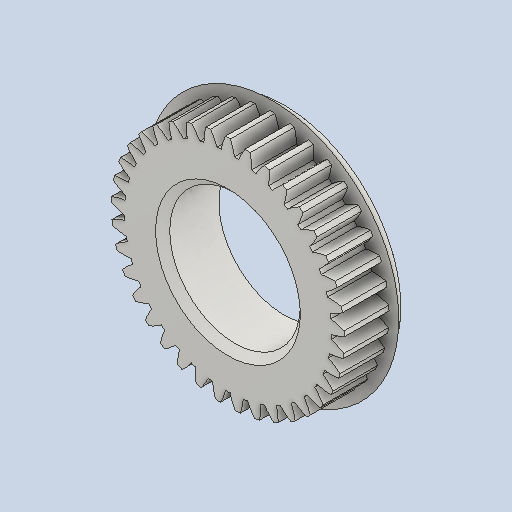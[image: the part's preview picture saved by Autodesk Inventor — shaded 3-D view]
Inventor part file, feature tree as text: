
AUTODESK INVENTOR PART (.ipt)
format: ipt  version: 2022 (Build 260153000, 153)  size: 615,936 bytes
history: native  units: in
note: dims shown in document units (in); Inventor stores cm internally (conversion verified against a paired STEP export)
features: other x12, sketch x4, plane x3
ambient origin geometry x8: Origin, YZ Plane, XZ Plane, XY Plane, X Axis, Y Axis, Z Axis, Center Point
bodies: Solid1 (feature_tree)
feature tree (19):
  other  "Spur Gear2"
  other  "Solid1::Spur Gear2"
  other  "TaggingFeature1"
  sketch  "Sketch1"  dims[d0=0.3937in]
  sketch  "Sketch2"  dims[d9=0.0in]
  sketch  "Sketch3"  dims[d14=0.0in]
  sketch  "Sketch4"  dims[d15=0.9352in d16=0.0in d17=0.0in d18=0.0in d19=0.9352in]
  plane  "XZ Plane_1"
  plane  "Work Plane2"
  plane  "Work Plane3"
  other  "Srf1"
  other  "Srf1::Derived"
  other  "Start plane iMate"
  other  "Distance iMate"
  other  "Position iMate"
  other  "Mesh iMate"
  other  "Axis iMate"
  other  "Mesh iMate2"
  other  "Align iMate"
